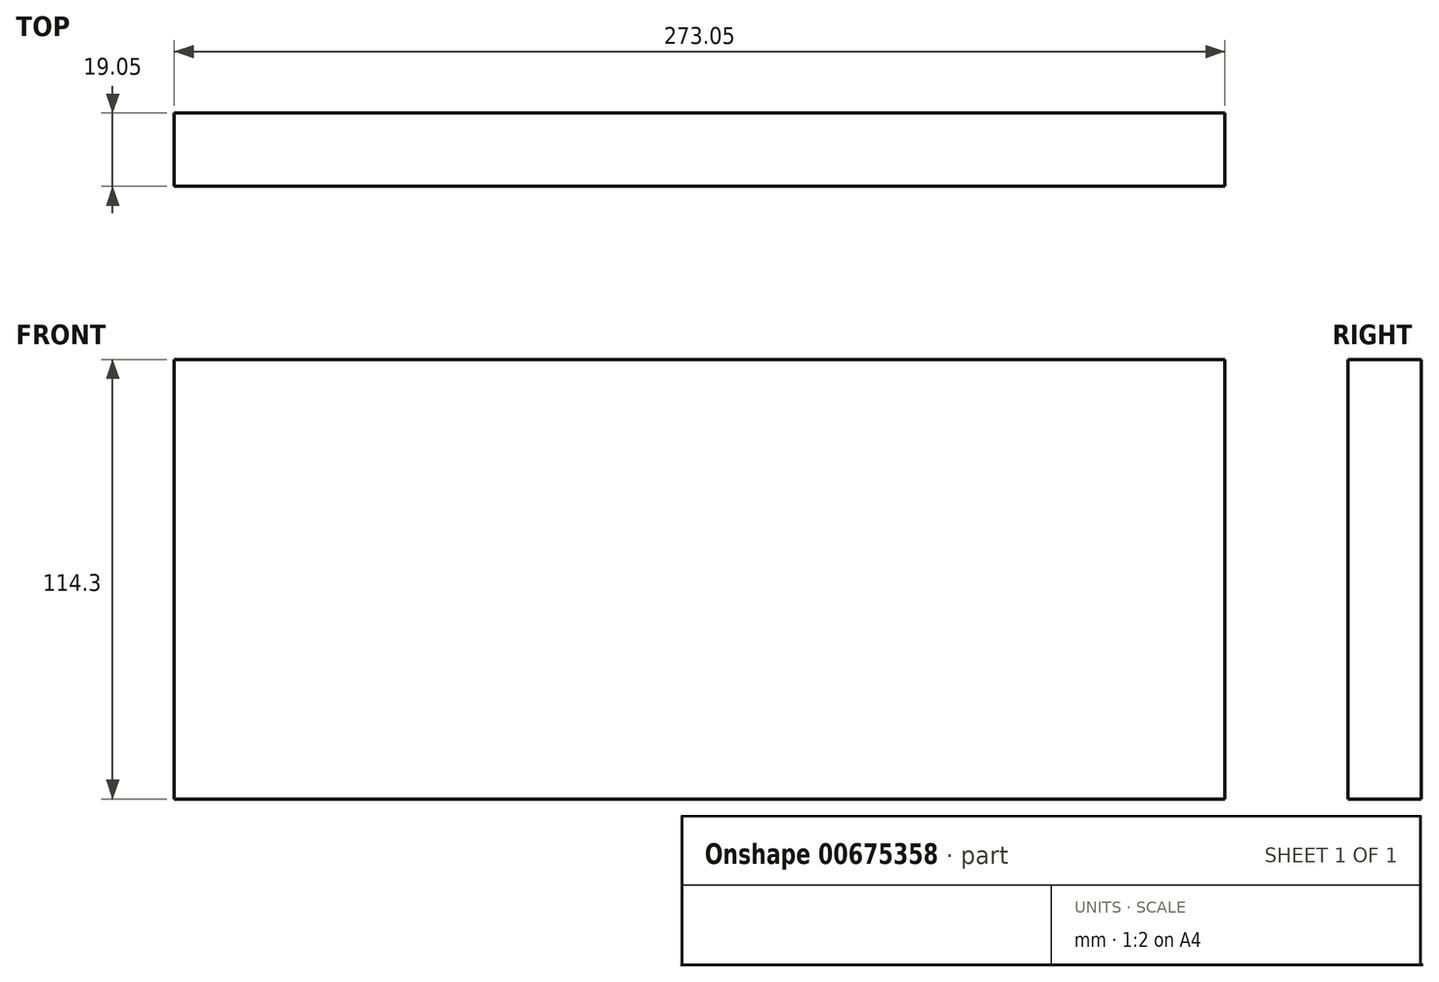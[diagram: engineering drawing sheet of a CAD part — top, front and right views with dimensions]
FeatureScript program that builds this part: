
annotation { "Feature Type Name" : "Feature", "Feature Type Description" : "" }
export const myFeature = defineFeature(function(context is Context, id is Id, definition is map)
    precondition{}
    {
        {
            var Q0;
            Q0=qCreatedBy(makeId("Front.planeOp"),FACE);
            var sketch = newSketch(context, id + "F0", { "sketchPlane" : qUnion([Q0])});
            skLineSegment(sketch, "E0.bottom", {"start": v(0, 0) * mm, "end": v(273.05, 0) * mm});
            skLineSegment(sketch, "E0.top", {"start": v(0, 114.3) * mm, "end": v(273.05, 114.3) * mm});
            skLineSegment(sketch, "E0.left", {"start": v(0, 0) * mm, "end": v(0, 114.3) * mm});
            skLineSegment(sketch, "E0.right", {"start": v(273.05, 0) * mm, "end": v(273.05, 114.3) * mm});
            skSolve(sketch);
        }
        {
            var Q0;
            Q0 = qSketchRegion(id + "F0", true);
            extrude(context, id + "F1", {"entities" : qUnion([Q0]), "depth" : 19.05 * mm, "offsetDistance" : 25.4 * mm});
        }
    });
